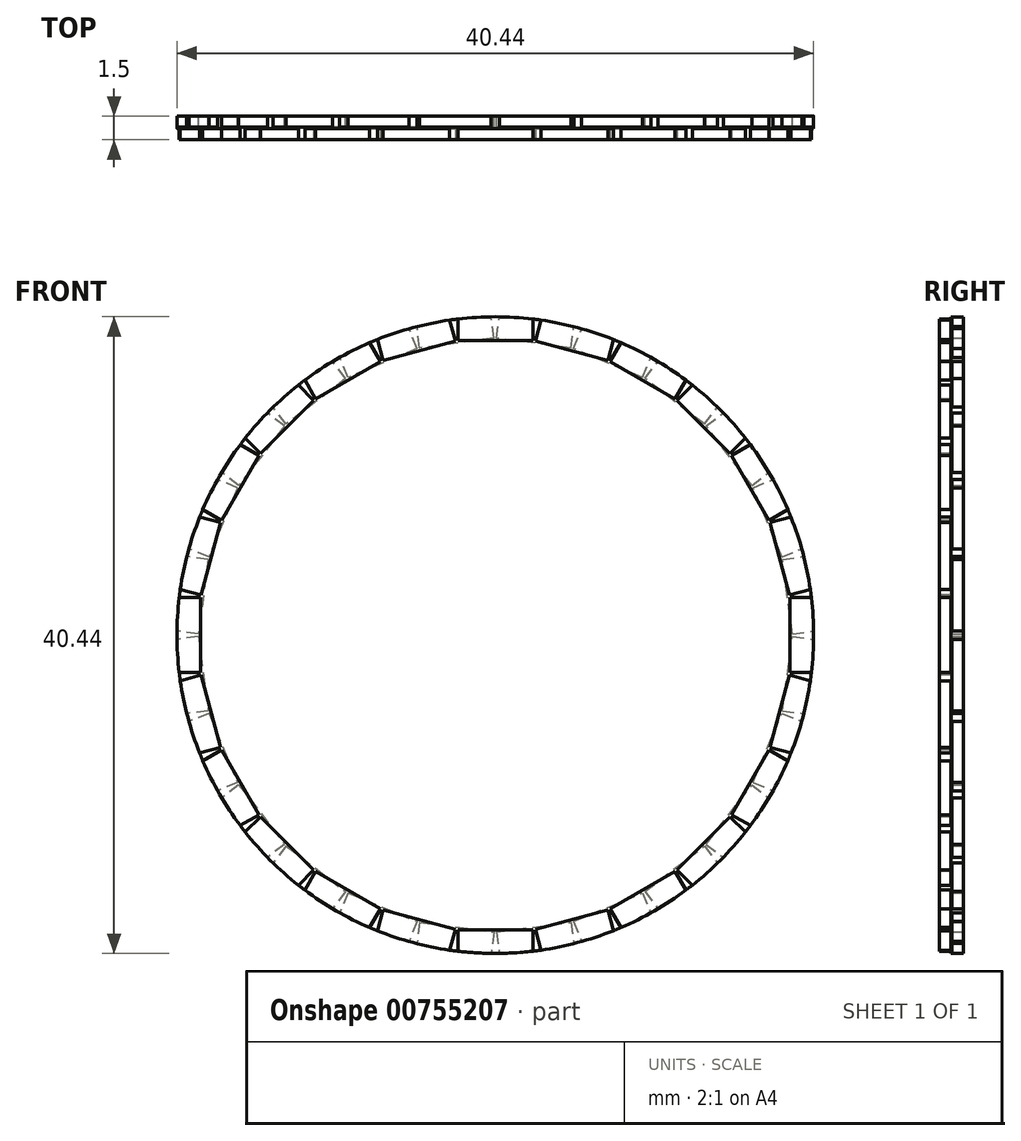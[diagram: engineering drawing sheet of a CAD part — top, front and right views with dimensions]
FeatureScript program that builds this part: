
annotation { "Feature Type Name" : "Feature", "Feature Type Description" : "" }
export const myFeature = defineFeature(function(context is Context, id is Id, definition is map)
    precondition{}
    {
        {
            var Q0;
            Q0=qCreatedBy(makeId("Front.planeOp"),FACE);
            var sketch = newSketch(context, id + "F0", { "sketchPlane" : qUnion([Q0])});
            skCircle(sketch, "E0", {"center": v(0, 0) * mm, "radius": 20.22 * mm});
            skSolve(sketch);
        }
        {
            var Q0;
            Q0 = qSketchRegion(id + "F0", true);
            extrude(context, id + "F1", {"entities" : qUnion([Q0]), "oppositeDirection" : true, "depth" : 1.5 * mm, "offsetDistance" : 25.4 * mm});
        }
        {
            var Q0;
            Q0=makeQuery(id+"F1.opExtrude","CAP_FACE",FACE,{"disambiguationData":[OSD([sQuery(id+"F0.wireOp",EDGE,"E0")])],"isStart":true});
            var sketch = newSketch(context, id + "F2", { "sketchPlane" : qUnion([Q0])});
            skCircle(sketch, "E1", {"center": v(0, 0) * mm, "radius": 18.86 * mm, "construction": true});
            skLineSegment(sketch, "E2", {"start": v(0, 0) * mm, "end": v(0, 13.24) * mm, "construction": true});
            skLineSegment(sketch, "E3", {"start": v(0, 18.7) * mm, "end": v(-2.38, 18.7) * mm});
            skLineSegment(sketch, "E4", {"start": v(0, 18.7) * mm, "end": v(2.38, 18.7) * mm});
            skLineSegment(sketch, "E5", {"start": v(-2.38, 18.7) * mm, "end": v(-2.38, 20.74) * mm});
            skLineSegment(sketch, "E6", {"start": v(-2.38, 20.74) * mm, "end": v(2.38, 20.74) * mm});
            skLineSegment(sketch, "E7", {"start": v(2.38, 20.74) * mm, "end": v(2.38, 18.7) * mm});
            skLineSegment(sketch, "E8.1.0", {"start": v(-4.84, 18.07) * mm, "end": v(-7.14, 17.45) * mm});
            skLineSegment(sketch, "E8.1.1", {"start": v(-4.84, 18.07) * mm, "end": v(-2.54, 18.69) * mm});
            skLineSegment(sketch, "E8.1.2", {"start": v(-7.14, 17.45) * mm, "end": v(-7.67, 19.42) * mm});
            skLineSegment(sketch, "E8.1.3", {"start": v(-7.67, 19.42) * mm, "end": v(-3.07, 20.65) * mm});
            skLineSegment(sketch, "E8.1.4", {"start": v(-3.07, 20.65) * mm, "end": v(-2.54, 18.69) * mm});
            skLineSegment(sketch, "E8.2.0", {"start": v(-9.35, 16.2) * mm, "end": v(-11.42, 15.01) * mm});
            skLineSegment(sketch, "E8.2.1", {"start": v(-9.35, 16.2) * mm, "end": v(-7.3, 17.4) * mm});
            skLineSegment(sketch, "E8.2.2", {"start": v(-11.42, 15.01) * mm, "end": v(-12.43, 16.77) * mm});
            skLineSegment(sketch, "E8.2.3", {"start": v(-12.43, 16.77) * mm, "end": v(-8.3, 19.15) * mm});
            skLineSegment(sketch, "E8.2.4", {"start": v(-8.3, 19.15) * mm, "end": v(-7.3, 17.4) * mm});
            skLineSegment(sketch, "E8.3.0", {"start": v(-13.23, 13.23) * mm, "end": v(-14.91, 11.55) * mm});
            skLineSegment(sketch, "E8.3.1", {"start": v(-13.23, 13.23) * mm, "end": v(-11.55, 14.91) * mm});
            skLineSegment(sketch, "E8.3.2", {"start": v(-14.91, 11.55) * mm, "end": v(-16.35, 12.98) * mm});
            skLineSegment(sketch, "E8.3.3", {"start": v(-16.35, 12.98) * mm, "end": v(-12.98, 16.35) * mm});
            skLineSegment(sketch, "E8.3.4", {"start": v(-12.98, 16.35) * mm, "end": v(-11.55, 14.91) * mm});
            skLineSegment(sketch, "E8.4.0", {"start": v(-16.2, 9.35) * mm, "end": v(-17.4, 7.3) * mm});
            skLineSegment(sketch, "E8.4.1", {"start": v(-16.2, 9.35) * mm, "end": v(-15.01, 11.42) * mm});
            skLineSegment(sketch, "E8.4.2", {"start": v(-17.4, 7.3) * mm, "end": v(-19.15, 8.3) * mm});
            skLineSegment(sketch, "E8.4.3", {"start": v(-19.15, 8.3) * mm, "end": v(-16.77, 12.43) * mm});
            skLineSegment(sketch, "E8.4.4", {"start": v(-16.77, 12.43) * mm, "end": v(-15.01, 11.42) * mm});
            skLineSegment(sketch, "E8.5.0", {"start": v(-18.07, 4.84) * mm, "end": v(-18.69, 2.54) * mm});
            skLineSegment(sketch, "E8.5.1", {"start": v(-18.07, 4.84) * mm, "end": v(-17.45, 7.14) * mm});
            skLineSegment(sketch, "E8.5.2", {"start": v(-18.69, 2.54) * mm, "end": v(-20.65, 3.07) * mm});
            skLineSegment(sketch, "E8.5.3", {"start": v(-20.65, 3.07) * mm, "end": v(-19.42, 7.67) * mm});
            skLineSegment(sketch, "E8.5.4", {"start": v(-19.42, 7.67) * mm, "end": v(-17.45, 7.14) * mm});
            skLineSegment(sketch, "E8.6.0", {"start": v(-18.7, 0) * mm, "end": v(-18.7, -2.38) * mm});
            skLineSegment(sketch, "E8.6.1", {"start": v(-18.7, 0) * mm, "end": v(-18.7, 2.38) * mm});
            skLineSegment(sketch, "E8.6.2", {"start": v(-18.7, -2.38) * mm, "end": v(-20.74, -2.38) * mm});
            skLineSegment(sketch, "E8.6.3", {"start": v(-20.74, -2.38) * mm, "end": v(-20.74, 2.38) * mm});
            skLineSegment(sketch, "E8.6.4", {"start": v(-20.74, 2.38) * mm, "end": v(-18.7, 2.38) * mm});
            skLineSegment(sketch, "E8.7.0", {"start": v(-18.07, -4.84) * mm, "end": v(-17.45, -7.14) * mm});
            skLineSegment(sketch, "E8.7.1", {"start": v(-18.07, -4.84) * mm, "end": v(-18.69, -2.54) * mm});
            skLineSegment(sketch, "E8.7.2", {"start": v(-17.45, -7.14) * mm, "end": v(-19.42, -7.67) * mm});
            skLineSegment(sketch, "E8.7.3", {"start": v(-19.42, -7.67) * mm, "end": v(-20.65, -3.07) * mm});
            skLineSegment(sketch, "E8.7.4", {"start": v(-20.65, -3.07) * mm, "end": v(-18.69, -2.54) * mm});
            skLineSegment(sketch, "E8.8.0", {"start": v(-16.2, -9.35) * mm, "end": v(-15.01, -11.42) * mm});
            skLineSegment(sketch, "E8.8.1", {"start": v(-16.2, -9.35) * mm, "end": v(-17.4, -7.3) * mm});
            skLineSegment(sketch, "E8.8.2", {"start": v(-15.01, -11.42) * mm, "end": v(-16.77, -12.43) * mm});
            skLineSegment(sketch, "E8.8.3", {"start": v(-16.77, -12.43) * mm, "end": v(-19.15, -8.3) * mm});
            skLineSegment(sketch, "E8.8.4", {"start": v(-19.15, -8.3) * mm, "end": v(-17.4, -7.3) * mm});
            skLineSegment(sketch, "E8.9.0", {"start": v(-13.23, -13.23) * mm, "end": v(-11.55, -14.91) * mm});
            skLineSegment(sketch, "E8.9.1", {"start": v(-13.23, -13.23) * mm, "end": v(-14.91, -11.55) * mm});
            skLineSegment(sketch, "E8.9.2", {"start": v(-11.55, -14.91) * mm, "end": v(-12.98, -16.35) * mm});
            skLineSegment(sketch, "E8.9.3", {"start": v(-12.98, -16.35) * mm, "end": v(-16.35, -12.98) * mm});
            skLineSegment(sketch, "E8.9.4", {"start": v(-16.35, -12.98) * mm, "end": v(-14.91, -11.55) * mm});
            skLineSegment(sketch, "E8.10.0", {"start": v(-9.35, -16.2) * mm, "end": v(-7.3, -17.4) * mm});
            skLineSegment(sketch, "E8.10.1", {"start": v(-9.35, -16.2) * mm, "end": v(-11.42, -15.01) * mm});
            skLineSegment(sketch, "E8.10.2", {"start": v(-7.3, -17.4) * mm, "end": v(-8.3, -19.15) * mm});
            skLineSegment(sketch, "E8.10.3", {"start": v(-8.3, -19.15) * mm, "end": v(-12.43, -16.77) * mm});
            skLineSegment(sketch, "E8.10.4", {"start": v(-12.43, -16.77) * mm, "end": v(-11.42, -15.01) * mm});
            skLineSegment(sketch, "E8.11.0", {"start": v(-4.84, -18.07) * mm, "end": v(-2.54, -18.69) * mm});
            skLineSegment(sketch, "E8.11.1", {"start": v(-4.84, -18.07) * mm, "end": v(-7.14, -17.45) * mm});
            skLineSegment(sketch, "E8.11.2", {"start": v(-2.54, -18.69) * mm, "end": v(-3.07, -20.65) * mm});
            skLineSegment(sketch, "E8.11.3", {"start": v(-3.07, -20.65) * mm, "end": v(-7.67, -19.42) * mm});
            skLineSegment(sketch, "E8.11.4", {"start": v(-7.67, -19.42) * mm, "end": v(-7.14, -17.45) * mm});
            skLineSegment(sketch, "E8.anchor1", {"start": v(0, 0) * mm, "end": v(-2.38, 18.7) * mm, "construction": true});
            skLineSegment(sketch, "E8.anchor2", {"start": v(0, 0) * mm, "end": v(2.54, 18.69) * mm, "construction": true});
            skLineSegment(sketch, "E9.2.12.0", {"start": v(0, -18.7) * mm, "end": v(2.38, -18.7) * mm});
            skLineSegment(sketch, "E9.3.12.0", {"start": v(0, -18.7) * mm, "end": v(-2.38, -18.7) * mm});
            skLineSegment(sketch, "E9.6.12.0", {"start": v(2.38, -18.7) * mm, "end": v(2.38, -20.74) * mm});
            skLineSegment(sketch, "E9.9.12.0", {"start": v(2.38, -20.74) * mm, "end": v(-2.38, -20.74) * mm});
            skLineSegment(sketch, "E9.12.12.0", {"start": v(-2.38, -20.74) * mm, "end": v(-2.38, -18.7) * mm});
            skLineSegment(sketch, "E9.2.13.0", {"start": v(4.84, -18.07) * mm, "end": v(7.14, -17.45) * mm});
            skLineSegment(sketch, "E9.3.13.0", {"start": v(4.84, -18.07) * mm, "end": v(2.54, -18.69) * mm});
            skLineSegment(sketch, "E9.6.13.0", {"start": v(7.14, -17.45) * mm, "end": v(7.67, -19.42) * mm});
            skLineSegment(sketch, "E9.9.13.0", {"start": v(7.67, -19.42) * mm, "end": v(3.07, -20.65) * mm});
            skLineSegment(sketch, "E9.12.13.0", {"start": v(3.07, -20.65) * mm, "end": v(2.54, -18.69) * mm});
            skLineSegment(sketch, "E9.2.14.0", {"start": v(9.35, -16.2) * mm, "end": v(11.42, -15.01) * mm});
            skLineSegment(sketch, "E9.3.14.0", {"start": v(9.35, -16.2) * mm, "end": v(7.3, -17.4) * mm});
            skLineSegment(sketch, "E9.6.14.0", {"start": v(11.42, -15.01) * mm, "end": v(12.43, -16.77) * mm});
            skLineSegment(sketch, "E9.9.14.0", {"start": v(12.43, -16.77) * mm, "end": v(8.3, -19.15) * mm});
            skLineSegment(sketch, "E9.12.14.0", {"start": v(8.3, -19.15) * mm, "end": v(7.3, -17.4) * mm});
            skLineSegment(sketch, "E9.2.15.0", {"start": v(13.23, -13.23) * mm, "end": v(14.91, -11.55) * mm});
            skLineSegment(sketch, "E9.3.15.0", {"start": v(13.23, -13.23) * mm, "end": v(11.55, -14.91) * mm});
            skLineSegment(sketch, "E9.6.15.0", {"start": v(14.91, -11.55) * mm, "end": v(16.35, -12.98) * mm});
            skLineSegment(sketch, "E9.9.15.0", {"start": v(16.35, -12.98) * mm, "end": v(12.98, -16.35) * mm});
            skLineSegment(sketch, "E9.12.15.0", {"start": v(12.98, -16.35) * mm, "end": v(11.55, -14.91) * mm});
            skLineSegment(sketch, "E9.2.16.0", {"start": v(16.2, -9.35) * mm, "end": v(17.4, -7.3) * mm});
            skLineSegment(sketch, "E9.3.16.0", {"start": v(16.2, -9.35) * mm, "end": v(15.01, -11.42) * mm});
            skLineSegment(sketch, "E9.6.16.0", {"start": v(17.4, -7.3) * mm, "end": v(19.15, -8.3) * mm});
            skLineSegment(sketch, "E9.9.16.0", {"start": v(19.15, -8.3) * mm, "end": v(16.77, -12.43) * mm});
            skLineSegment(sketch, "E9.12.16.0", {"start": v(16.77, -12.43) * mm, "end": v(15.01, -11.42) * mm});
            skLineSegment(sketch, "E9.2.17.0", {"start": v(18.07, -4.84) * mm, "end": v(18.69, -2.54) * mm});
            skLineSegment(sketch, "E9.3.17.0", {"start": v(18.07, -4.84) * mm, "end": v(17.45, -7.14) * mm});
            skLineSegment(sketch, "E9.6.17.0", {"start": v(18.69, -2.54) * mm, "end": v(20.65, -3.07) * mm});
            skLineSegment(sketch, "E9.9.17.0", {"start": v(20.65, -3.07) * mm, "end": v(19.42, -7.67) * mm});
            skLineSegment(sketch, "E9.12.17.0", {"start": v(19.42, -7.67) * mm, "end": v(17.45, -7.14) * mm});
            skLineSegment(sketch, "E9.2.18.0", {"start": v(18.7, 0) * mm, "end": v(18.7, 2.38) * mm});
            skLineSegment(sketch, "E9.3.18.0", {"start": v(18.7, 0) * mm, "end": v(18.7, -2.38) * mm});
            skLineSegment(sketch, "E9.6.18.0", {"start": v(18.7, 2.38) * mm, "end": v(20.74, 2.38) * mm});
            skLineSegment(sketch, "E9.9.18.0", {"start": v(20.74, 2.38) * mm, "end": v(20.74, -2.38) * mm});
            skLineSegment(sketch, "E9.12.18.0", {"start": v(20.74, -2.38) * mm, "end": v(18.7, -2.38) * mm});
            skLineSegment(sketch, "E9.2.19.0", {"start": v(18.07, 4.84) * mm, "end": v(17.45, 7.14) * mm});
            skLineSegment(sketch, "E9.3.19.0", {"start": v(18.07, 4.84) * mm, "end": v(18.69, 2.54) * mm});
            skLineSegment(sketch, "E9.6.19.0", {"start": v(17.45, 7.14) * mm, "end": v(19.42, 7.67) * mm});
            skLineSegment(sketch, "E9.9.19.0", {"start": v(19.42, 7.67) * mm, "end": v(20.65, 3.07) * mm});
            skLineSegment(sketch, "E9.12.19.0", {"start": v(20.65, 3.07) * mm, "end": v(18.69, 2.54) * mm});
            skLineSegment(sketch, "E9.2.20.0", {"start": v(16.2, 9.35) * mm, "end": v(15.01, 11.42) * mm});
            skLineSegment(sketch, "E9.3.20.0", {"start": v(16.2, 9.35) * mm, "end": v(17.4, 7.3) * mm});
            skLineSegment(sketch, "E9.6.20.0", {"start": v(15.01, 11.42) * mm, "end": v(16.77, 12.43) * mm});
            skLineSegment(sketch, "E9.9.20.0", {"start": v(16.77, 12.43) * mm, "end": v(19.15, 8.3) * mm});
            skLineSegment(sketch, "E9.12.20.0", {"start": v(19.15, 8.3) * mm, "end": v(17.4, 7.3) * mm});
            skLineSegment(sketch, "E9.2.21.0", {"start": v(13.23, 13.23) * mm, "end": v(11.55, 14.91) * mm});
            skLineSegment(sketch, "E9.3.21.0", {"start": v(13.23, 13.23) * mm, "end": v(14.91, 11.55) * mm});
            skLineSegment(sketch, "E9.6.21.0", {"start": v(11.55, 14.91) * mm, "end": v(12.98, 16.35) * mm});
            skLineSegment(sketch, "E9.9.21.0", {"start": v(12.98, 16.35) * mm, "end": v(16.35, 12.98) * mm});
            skLineSegment(sketch, "E9.12.21.0", {"start": v(16.35, 12.98) * mm, "end": v(14.91, 11.55) * mm});
            skLineSegment(sketch, "E9.2.22.0", {"start": v(9.35, 16.2) * mm, "end": v(7.3, 17.4) * mm});
            skLineSegment(sketch, "E9.3.22.0", {"start": v(9.35, 16.2) * mm, "end": v(11.42, 15.01) * mm});
            skLineSegment(sketch, "E9.6.22.0", {"start": v(7.3, 17.4) * mm, "end": v(8.3, 19.15) * mm});
            skLineSegment(sketch, "E9.9.22.0", {"start": v(8.3, 19.15) * mm, "end": v(12.43, 16.77) * mm});
            skLineSegment(sketch, "E9.12.22.0", {"start": v(12.43, 16.77) * mm, "end": v(11.42, 15.01) * mm});
            skLineSegment(sketch, "E9.2.23.0", {"start": v(4.84, 18.07) * mm, "end": v(2.54, 18.69) * mm});
            skLineSegment(sketch, "E9.3.23.0", {"start": v(4.84, 18.07) * mm, "end": v(7.14, 17.45) * mm});
            skLineSegment(sketch, "E9.6.23.0", {"start": v(2.54, 18.69) * mm, "end": v(3.07, 20.65) * mm});
            skLineSegment(sketch, "E9.9.23.0", {"start": v(3.07, 20.65) * mm, "end": v(7.67, 19.42) * mm});
            skLineSegment(sketch, "E9.12.23.0", {"start": v(7.67, 19.42) * mm, "end": v(7.14, 17.45) * mm});
            skSolve(sketch);
        }
        {
            var Q0;
            Q0 = qSketchRegion(id + "F2", true);
            extrude(context, id + "F3", {"entities" : qUnion([Q0]), "operationType" : NewBodyOperationType.REMOVE, "oppositeDirection" : true, "depth" : 0.71 * mm, "offsetDistance" : 25.4 * mm});
        }
        {
            var Q0;
            Q0=makeQuery(id+"F1.opExtrude","CAP_FACE",FACE,{"disambiguationData":[OSD([sQuery(id+"F0.wireOp",EDGE,"E0")])],"isStart":false});
            var sketch = newSketch(context, id + "F4", { "sketchPlane" : qUnion([Q0])});
            skLineSegment(sketch, "E10", {"start": v(0, 0) * mm, "end": v(1.9, 14.4) * mm, "construction": true});
            skArc(sketch, "E11", {"start": v(4.8, 18.24) * mm, "mid": v(2.46, 18.7) * mm, "end": v(0.08, 18.86) * mm, "construction": true});
            skLineSegment(sketch, "E12", {"start": v(0.08, 18.86) * mm, "end": v(0.37, 21.02) * mm});
            skLineSegment(sketch, "E13", {"start": v(4.8, 18.24) * mm, "end": v(5.09, 20.4) * mm});
            skLineSegment(sketch, "E14", {"start": v(0.37, 21.02) * mm, "end": v(5.09, 20.4) * mm});
            skLineSegment(sketch, "E15.anchor1", {"start": v(0, 0) * mm, "end": v(0, 13.02) * mm, "construction": true});
            skLineSegment(sketch, "E16", {"start": v(0.08, 18.86) * mm, "end": v(2.44, 18.55) * mm});
            skLineSegment(sketch, "E17", {"start": v(2.44, 18.55) * mm, "end": v(4.8, 18.24) * mm});
            skLineSegment(sketch, "E18.1.0", {"start": v(-4.8, 18.24) * mm, "end": v(-5.09, 20.4) * mm});
            skLineSegment(sketch, "E18.1.1", {"start": v(-5.09, 20.4) * mm, "end": v(-0.37, 21.02) * mm});
            skLineSegment(sketch, "E18.1.2", {"start": v(-0.08, 18.86) * mm, "end": v(-0.37, 21.02) * mm});
            skLineSegment(sketch, "E18.1.3", {"start": v(-4.8, 18.24) * mm, "end": v(-2.44, 18.55) * mm});
            skLineSegment(sketch, "E18.1.4", {"start": v(-2.44, 18.55) * mm, "end": v(-0.08, 18.86) * mm});
            skLineSegment(sketch, "E18.2.0", {"start": v(-9.36, 16.37) * mm, "end": v(-10.2, 18.39) * mm});
            skLineSegment(sketch, "E18.2.1", {"start": v(-10.2, 18.39) * mm, "end": v(-5.8, 20.21) * mm});
            skLineSegment(sketch, "E18.2.2", {"start": v(-4.96, 18.2) * mm, "end": v(-5.8, 20.21) * mm});
            skLineSegment(sketch, "E18.2.3", {"start": v(-9.36, 16.37) * mm, "end": v(-7.16, 17.28) * mm});
            skLineSegment(sketch, "E18.2.4", {"start": v(-7.16, 17.28) * mm, "end": v(-4.96, 18.2) * mm});
            skLineSegment(sketch, "E18.3.0", {"start": v(-13.28, 13.4) * mm, "end": v(-14.6, 15.12) * mm});
            skLineSegment(sketch, "E18.3.1", {"start": v(-14.6, 15.12) * mm, "end": v(-10.83, 18.02) * mm});
            skLineSegment(sketch, "E18.3.2", {"start": v(-9.5, 16.3) * mm, "end": v(-10.83, 18.02) * mm});
            skLineSegment(sketch, "E18.3.3", {"start": v(-13.28, 13.4) * mm, "end": v(-11.39, 14.84) * mm});
            skLineSegment(sketch, "E18.3.4", {"start": v(-11.39, 14.84) * mm, "end": v(-9.5, 16.3) * mm});
            skLineSegment(sketch, "E18.4.0", {"start": v(-16.3, 9.5) * mm, "end": v(-18.02, 10.83) * mm});
            skLineSegment(sketch, "E18.4.1", {"start": v(-18.02, 10.83) * mm, "end": v(-15.12, 14.6) * mm});
            skLineSegment(sketch, "E18.4.2", {"start": v(-13.4, 13.28) * mm, "end": v(-15.12, 14.6) * mm});
            skLineSegment(sketch, "E18.4.3", {"start": v(-16.3, 9.5) * mm, "end": v(-14.84, 11.39) * mm});
            skLineSegment(sketch, "E18.4.4", {"start": v(-14.84, 11.39) * mm, "end": v(-13.4, 13.28) * mm});
            skLineSegment(sketch, "E18.5.0", {"start": v(-18.2, 4.96) * mm, "end": v(-20.21, 5.8) * mm});
            skLineSegment(sketch, "E18.5.1", {"start": v(-20.21, 5.8) * mm, "end": v(-18.39, 10.2) * mm});
            skLineSegment(sketch, "E18.5.2", {"start": v(-16.37, 9.36) * mm, "end": v(-18.39, 10.2) * mm});
            skLineSegment(sketch, "E18.5.3", {"start": v(-18.2, 4.96) * mm, "end": v(-17.28, 7.16) * mm});
            skLineSegment(sketch, "E18.5.4", {"start": v(-17.28, 7.16) * mm, "end": v(-16.37, 9.36) * mm});
            skLineSegment(sketch, "E18.6.0", {"start": v(-18.86, 0.08) * mm, "end": v(-21.02, 0.37) * mm});
            skLineSegment(sketch, "E18.6.1", {"start": v(-21.02, 0.37) * mm, "end": v(-20.4, 5.09) * mm});
            skLineSegment(sketch, "E18.6.2", {"start": v(-18.24, 4.8) * mm, "end": v(-20.4, 5.09) * mm});
            skLineSegment(sketch, "E18.6.3", {"start": v(-18.86, 0.08) * mm, "end": v(-18.55, 2.44) * mm});
            skLineSegment(sketch, "E18.6.4", {"start": v(-18.55, 2.44) * mm, "end": v(-18.24, 4.8) * mm});
            skLineSegment(sketch, "E18.7.0", {"start": v(-18.24, -4.8) * mm, "end": v(-20.4, -5.09) * mm});
            skLineSegment(sketch, "E18.7.1", {"start": v(-20.4, -5.09) * mm, "end": v(-21.02, -0.37) * mm});
            skLineSegment(sketch, "E18.7.2", {"start": v(-18.86, -0.08) * mm, "end": v(-21.02, -0.37) * mm});
            skLineSegment(sketch, "E18.7.3", {"start": v(-18.24, -4.8) * mm, "end": v(-18.55, -2.44) * mm});
            skLineSegment(sketch, "E18.7.4", {"start": v(-18.55, -2.44) * mm, "end": v(-18.86, -0.08) * mm});
            skLineSegment(sketch, "E18.8.0", {"start": v(-16.37, -9.36) * mm, "end": v(-18.39, -10.2) * mm});
            skLineSegment(sketch, "E18.8.1", {"start": v(-18.39, -10.2) * mm, "end": v(-20.21, -5.8) * mm});
            skLineSegment(sketch, "E18.8.2", {"start": v(-18.2, -4.96) * mm, "end": v(-20.21, -5.8) * mm});
            skLineSegment(sketch, "E18.8.3", {"start": v(-16.37, -9.36) * mm, "end": v(-17.28, -7.16) * mm});
            skLineSegment(sketch, "E18.8.4", {"start": v(-17.28, -7.16) * mm, "end": v(-18.2, -4.96) * mm});
            skLineSegment(sketch, "E18.9.0", {"start": v(-13.4, -13.28) * mm, "end": v(-15.12, -14.6) * mm});
            skLineSegment(sketch, "E18.9.1", {"start": v(-15.12, -14.6) * mm, "end": v(-18.02, -10.83) * mm});
            skLineSegment(sketch, "E18.9.2", {"start": v(-16.3, -9.5) * mm, "end": v(-18.02, -10.83) * mm});
            skLineSegment(sketch, "E18.9.3", {"start": v(-13.4, -13.28) * mm, "end": v(-14.84, -11.39) * mm});
            skLineSegment(sketch, "E18.9.4", {"start": v(-14.84, -11.39) * mm, "end": v(-16.3, -9.5) * mm});
            skLineSegment(sketch, "E18.10.0", {"start": v(-9.5, -16.3) * mm, "end": v(-10.83, -18.02) * mm});
            skLineSegment(sketch, "E18.10.1", {"start": v(-10.83, -18.02) * mm, "end": v(-14.6, -15.12) * mm});
            skLineSegment(sketch, "E18.10.2", {"start": v(-13.28, -13.4) * mm, "end": v(-14.6, -15.12) * mm});
            skLineSegment(sketch, "E18.10.3", {"start": v(-9.5, -16.3) * mm, "end": v(-11.39, -14.84) * mm});
            skLineSegment(sketch, "E18.10.4", {"start": v(-11.39, -14.84) * mm, "end": v(-13.28, -13.4) * mm});
            skLineSegment(sketch, "E18.11.0", {"start": v(-4.96, -18.2) * mm, "end": v(-5.8, -20.21) * mm});
            skLineSegment(sketch, "E18.11.1", {"start": v(-5.8, -20.21) * mm, "end": v(-10.2, -18.39) * mm});
            skLineSegment(sketch, "E18.11.2", {"start": v(-9.36, -16.37) * mm, "end": v(-10.2, -18.39) * mm});
            skLineSegment(sketch, "E18.11.3", {"start": v(-4.96, -18.2) * mm, "end": v(-7.16, -17.28) * mm});
            skLineSegment(sketch, "E18.11.4", {"start": v(-7.16, -17.28) * mm, "end": v(-9.36, -16.37) * mm});
            skCircle(sketch, "E19", {"center": v(0, 0) * mm, "radius": 18.86 * mm, "construction": true});
            skLineSegment(sketch, "E20.1.12.0", {"start": v(-0.08, -18.86) * mm, "end": v(-0.37, -21.02) * mm});
            skLineSegment(sketch, "E20.3.12.0", {"start": v(-0.37, -21.02) * mm, "end": v(-5.09, -20.4) * mm});
            skLineSegment(sketch, "E20.6.12.0", {"start": v(-4.8, -18.24) * mm, "end": v(-5.09, -20.4) * mm});
            skLineSegment(sketch, "E20.9.12.0", {"start": v(-0.08, -18.86) * mm, "end": v(-2.44, -18.55) * mm});
            skLineSegment(sketch, "E20.12.12.0", {"start": v(-2.44, -18.55) * mm, "end": v(-4.8, -18.24) * mm});
            skLineSegment(sketch, "E20.1.13.0", {"start": v(4.8, -18.24) * mm, "end": v(5.09, -20.4) * mm});
            skLineSegment(sketch, "E20.3.13.0", {"start": v(5.09, -20.4) * mm, "end": v(0.37, -21.02) * mm});
            skLineSegment(sketch, "E20.6.13.0", {"start": v(0.08, -18.86) * mm, "end": v(0.37, -21.02) * mm});
            skLineSegment(sketch, "E20.9.13.0", {"start": v(4.8, -18.24) * mm, "end": v(2.44, -18.55) * mm});
            skLineSegment(sketch, "E20.12.13.0", {"start": v(2.44, -18.55) * mm, "end": v(0.08, -18.86) * mm});
            skLineSegment(sketch, "E20.1.14.0", {"start": v(9.36, -16.37) * mm, "end": v(10.2, -18.39) * mm});
            skLineSegment(sketch, "E20.3.14.0", {"start": v(10.2, -18.39) * mm, "end": v(5.8, -20.21) * mm});
            skLineSegment(sketch, "E20.6.14.0", {"start": v(4.96, -18.2) * mm, "end": v(5.8, -20.21) * mm});
            skLineSegment(sketch, "E20.9.14.0", {"start": v(9.36, -16.37) * mm, "end": v(7.16, -17.28) * mm});
            skLineSegment(sketch, "E20.12.14.0", {"start": v(7.16, -17.28) * mm, "end": v(4.96, -18.2) * mm});
            skLineSegment(sketch, "E20.1.15.0", {"start": v(13.28, -13.4) * mm, "end": v(14.6, -15.12) * mm});
            skLineSegment(sketch, "E20.3.15.0", {"start": v(14.6, -15.12) * mm, "end": v(10.83, -18.02) * mm});
            skLineSegment(sketch, "E20.6.15.0", {"start": v(9.5, -16.3) * mm, "end": v(10.83, -18.02) * mm});
            skLineSegment(sketch, "E20.9.15.0", {"start": v(13.28, -13.4) * mm, "end": v(11.39, -14.84) * mm});
            skLineSegment(sketch, "E20.12.15.0", {"start": v(11.39, -14.84) * mm, "end": v(9.5, -16.3) * mm});
            skLineSegment(sketch, "E20.1.16.0", {"start": v(16.3, -9.5) * mm, "end": v(18.02, -10.83) * mm});
            skLineSegment(sketch, "E20.3.16.0", {"start": v(18.02, -10.83) * mm, "end": v(15.12, -14.6) * mm});
            skLineSegment(sketch, "E20.6.16.0", {"start": v(13.4, -13.28) * mm, "end": v(15.12, -14.6) * mm});
            skLineSegment(sketch, "E20.9.16.0", {"start": v(16.3, -9.5) * mm, "end": v(14.84, -11.39) * mm});
            skLineSegment(sketch, "E20.12.16.0", {"start": v(14.84, -11.39) * mm, "end": v(13.4, -13.28) * mm});
            skLineSegment(sketch, "E20.1.17.0", {"start": v(18.2, -4.96) * mm, "end": v(20.21, -5.8) * mm});
            skLineSegment(sketch, "E20.3.17.0", {"start": v(20.21, -5.8) * mm, "end": v(18.39, -10.2) * mm});
            skLineSegment(sketch, "E20.6.17.0", {"start": v(16.37, -9.36) * mm, "end": v(18.39, -10.2) * mm});
            skLineSegment(sketch, "E20.9.17.0", {"start": v(18.2, -4.96) * mm, "end": v(17.28, -7.16) * mm});
            skLineSegment(sketch, "E20.12.17.0", {"start": v(17.28, -7.16) * mm, "end": v(16.37, -9.36) * mm});
            skLineSegment(sketch, "E20.1.18.0", {"start": v(18.86, -0.08) * mm, "end": v(21.02, -0.37) * mm});
            skLineSegment(sketch, "E20.3.18.0", {"start": v(21.02, -0.37) * mm, "end": v(20.4, -5.09) * mm});
            skLineSegment(sketch, "E20.6.18.0", {"start": v(18.24, -4.8) * mm, "end": v(20.4, -5.09) * mm});
            skLineSegment(sketch, "E20.9.18.0", {"start": v(18.86, -0.08) * mm, "end": v(18.55, -2.44) * mm});
            skLineSegment(sketch, "E20.12.18.0", {"start": v(18.55, -2.44) * mm, "end": v(18.24, -4.8) * mm});
            skLineSegment(sketch, "E20.1.19.0", {"start": v(18.24, 4.8) * mm, "end": v(20.4, 5.09) * mm});
            skLineSegment(sketch, "E20.3.19.0", {"start": v(20.4, 5.09) * mm, "end": v(21.02, 0.37) * mm});
            skLineSegment(sketch, "E20.6.19.0", {"start": v(18.86, 0.08) * mm, "end": v(21.02, 0.37) * mm});
            skLineSegment(sketch, "E20.9.19.0", {"start": v(18.24, 4.8) * mm, "end": v(18.55, 2.44) * mm});
            skLineSegment(sketch, "E20.12.19.0", {"start": v(18.55, 2.44) * mm, "end": v(18.86, 0.08) * mm});
            skLineSegment(sketch, "E20.1.20.0", {"start": v(16.37, 9.36) * mm, "end": v(18.39, 10.2) * mm});
            skLineSegment(sketch, "E20.3.20.0", {"start": v(18.39, 10.2) * mm, "end": v(20.21, 5.8) * mm});
            skLineSegment(sketch, "E20.6.20.0", {"start": v(18.2, 4.96) * mm, "end": v(20.21, 5.8) * mm});
            skLineSegment(sketch, "E20.9.20.0", {"start": v(16.37, 9.36) * mm, "end": v(17.28, 7.16) * mm});
            skLineSegment(sketch, "E20.12.20.0", {"start": v(17.28, 7.16) * mm, "end": v(18.2, 4.96) * mm});
            skLineSegment(sketch, "E20.1.21.0", {"start": v(13.4, 13.28) * mm, "end": v(15.12, 14.6) * mm});
            skLineSegment(sketch, "E20.3.21.0", {"start": v(15.12, 14.6) * mm, "end": v(18.02, 10.83) * mm});
            skLineSegment(sketch, "E20.6.21.0", {"start": v(16.3, 9.5) * mm, "end": v(18.02, 10.83) * mm});
            skLineSegment(sketch, "E20.9.21.0", {"start": v(13.4, 13.28) * mm, "end": v(14.84, 11.39) * mm});
            skLineSegment(sketch, "E20.12.21.0", {"start": v(14.84, 11.39) * mm, "end": v(16.3, 9.5) * mm});
            skLineSegment(sketch, "E20.1.22.0", {"start": v(9.5, 16.3) * mm, "end": v(10.83, 18.02) * mm});
            skLineSegment(sketch, "E20.3.22.0", {"start": v(10.83, 18.02) * mm, "end": v(14.6, 15.12) * mm});
            skLineSegment(sketch, "E20.6.22.0", {"start": v(13.28, 13.4) * mm, "end": v(14.6, 15.12) * mm});
            skLineSegment(sketch, "E20.9.22.0", {"start": v(9.5, 16.3) * mm, "end": v(11.39, 14.84) * mm});
            skLineSegment(sketch, "E20.12.22.0", {"start": v(11.39, 14.84) * mm, "end": v(13.28, 13.4) * mm});
            skLineSegment(sketch, "E20.1.23.0", {"start": v(4.96, 18.2) * mm, "end": v(5.8, 20.21) * mm});
            skLineSegment(sketch, "E20.3.23.0", {"start": v(5.8, 20.21) * mm, "end": v(10.2, 18.39) * mm});
            skLineSegment(sketch, "E20.6.23.0", {"start": v(9.36, 16.37) * mm, "end": v(10.2, 18.39) * mm});
            skLineSegment(sketch, "E20.9.23.0", {"start": v(4.96, 18.2) * mm, "end": v(7.16, 17.28) * mm});
            skLineSegment(sketch, "E20.12.23.0", {"start": v(7.16, 17.28) * mm, "end": v(9.36, 16.37) * mm});
            skSolve(sketch);
        }
        {
            var Q0;
            Q0 = qSketchRegion(id + "F4", true);
            extrude(context, id + "F5", {"entities" : qUnion([Q0]), "operationType" : NewBodyOperationType.REMOVE, "oppositeDirection" : true, "depth" : 0.71 * mm, "offsetDistance" : 25.4 * mm});
        }
    });
